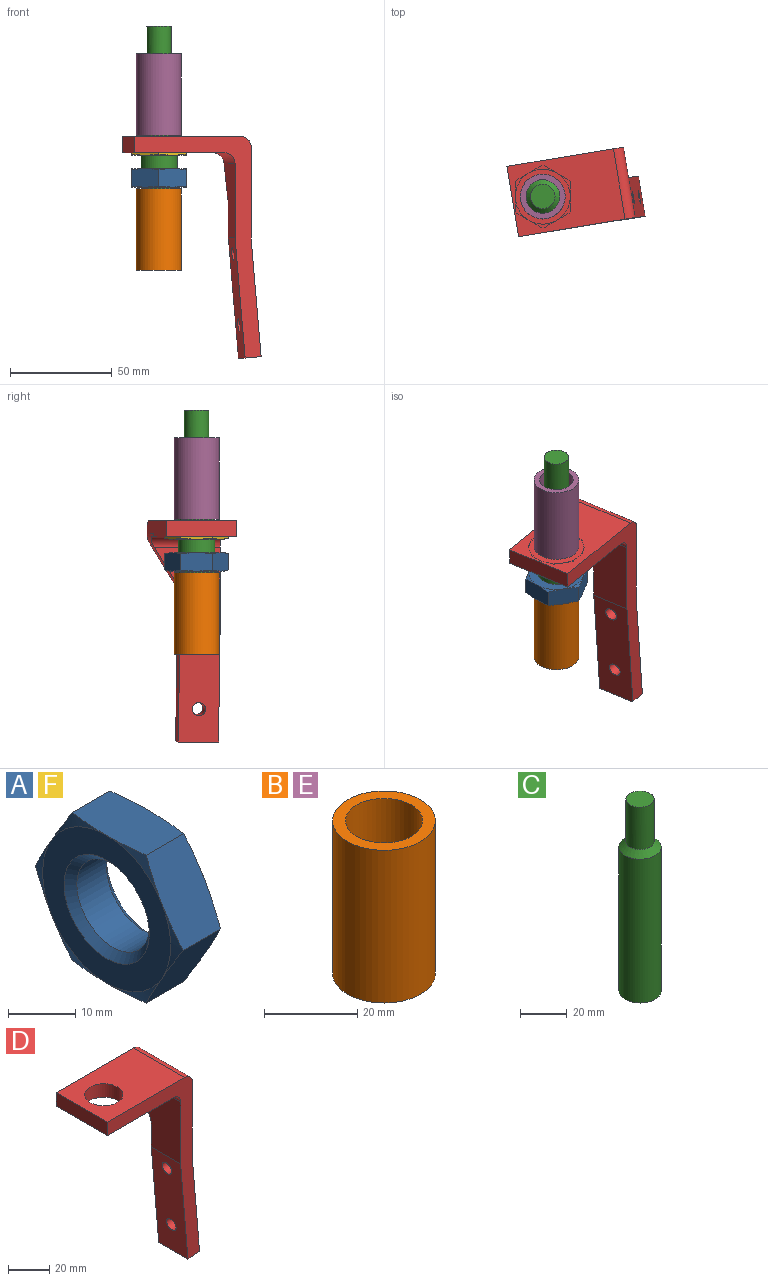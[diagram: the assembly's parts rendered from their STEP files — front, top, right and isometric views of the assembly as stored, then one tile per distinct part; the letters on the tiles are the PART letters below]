
ASSEMBLY  parts=6 mates=5
PART A: 23 faces, bbox 10.2x32.3x32.3 mm
  f0: cone r=13.5mm half-angle=75deg, axis (-1,0,0), area 16.1mm2, adj f14,f17,f22
  f1: cone r=13.5mm half-angle=75deg, axis (-1,0,0), area 16.1mm2, adj f14,f17,f18
  f2: cone r=13.5mm half-angle=75deg, axis (-1,0,0), area 16.1mm2, adj f14,f18,f19
  f3: cone r=13.5mm half-angle=75deg, axis (-1,0,0), area 16.1mm2, adj f14,f19,f20
  f4: cone r=13.5mm half-angle=75deg, axis (-1,0,0), area 16.1mm2, adj f14,f20,f21
  f5: cone r=30.29mm half-angle=75deg, axis (1,0,0), area 16.1mm2, adj f10,f19,f20
  f6: cone r=30.29mm half-angle=75deg, axis (1,0,0), area 16.1mm2, adj f10,f18,f19
  f7: cone r=30.29mm half-angle=75deg, axis (1,0,0), area 16.1mm2, adj f10,f17,f18
  f8: cone r=30.29mm half-angle=75deg, axis (1,0,0), area 16.1mm2, adj f10,f20,f21
  f9: cone r=30.29mm half-angle=75deg, axis (1,0,0), area 16.1mm2, adj f10,f17,f22
  f10: plane 27x27mm, normal (-1,0,0), area 318.1mm2, adj f5,f6,f7,f8,f9,f11,f16
  f11: cone r=9mm half-angle=45deg, axis (-1,0,0), area 100.1mm2, adj f10,f12
  f12: cylinder r=7.65mm len=15.29mm, axis (1,0,0), area 302.4mm2, adj f11,f13
  f13: cone r=7.65mm half-angle=45deg, axis (1,0,0), area 100.1mm2, adj f12,f14
  f14: plane 27x27mm, normal (1,0,0), area 318.1mm2, adj f0,f1,f2,f3,f4,f13,f15
  f15: cone r=13.5mm half-angle=75deg, axis (-1,0,0), area 16.1mm2, adj f14,f21,f22
  f16: cone r=30.29mm half-angle=75deg, axis (1,0,0), area 16.1mm2, adj f10,f21,f22
  f17: plane 16.75x10.16mm, normal (0,0,1), area 134.3mm2, adj f0,f1,f7,f9,f18,f22
  f18: plane 14.66x10.16mm, normal (0,0.87,0.5), area 134.3mm2, adj f1,f2,f6,f7,f17,f19
  f19: plane 14.66x10.16mm, normal (0,0.87,-0.5), area 134.3mm2, adj f2,f3,f5,f6,f18,f20
  f20: plane 16.75x10.16mm, normal (0,0,-1), area 134.3mm2, adj f3,f4,f5,f8,f19,f21
  f21: plane 14.66x10.16mm, normal (0,-0.87,-0.5), area 134.3mm2, adj f4,f8,f15,f16,f20,f22
  f22: plane 14.66x10.16mm, normal (0,-0.87,0.5), area 134.3mm2, adj f0,f9,f15,f16,f17,f21
PART B: 4 faces, bbox 22x22x40 mm
  f0: cylinder r=11mm len=40mm, axis (0,0,-1), area 2764.6mm2, adj f1,f2
  f1: plane 22x22mm, normal (0,0,1), area 166.3mm2, adj f0,f3
  f2: plane 22x22mm, normal (0,0,-1), area 166.3mm2, adj f0,f3
  f3: cylinder r=8.25mm len=40mm, axis (0,0,1), area 2073.5mm2, adj f1,f2
PART C: 5 faces, bbox 18x18x100 mm
  f0: cylinder r=9mm len=75mm, axis (0,0,-1), area 4241.2mm2, adj f1,f4
  f1: plane 18x18mm, normal (0,0,-1), area 254.5mm2, adj f0
  f2: cylinder r=6mm len=22mm, axis (0,0,1), area 829.4mm2, adj f3,f4
  f3: plane 12x12mm, normal (0,0,1), area 113.1mm2, adj f2
  f4: cone r=4mm half-angle=45deg, axis (0,0,-1), area 199.9mm2, adj f0,f2
PART D: 20 faces, bbox 63x35x108.7 mm
  f0: plane 45x35mm, normal (0,0,-1), area 1305.4mm2, adj f1,f7,f10,f11,f17,f18,f19
  f1: cylinder r=5mm len=34.88mm, axis (0,1,0), area 269.2mm2, adj f0,f2,f11,f15,f17
  f2: plane 36.78x32.72mm, normal (-1,0,0), area 866.4mm2, adj f1,f3,f11,f14,f15,f16
  f3: plane 58.91x20mm, normal (-1,0,-0.09), area 1116.1mm2, adj f2,f4,f11,f12,f13,f14
  f4: plane 20x7.97mm, normal (0.09,0,-1), area 160mm2, adj f3,f5,f11,f14
  f5: plane 58.22x20mm, normal (1,0,0.09), area 1102.4mm2, adj f4,f6,f11,f12,f13,f14
  f6: plane 44.78x35mm, normal (1,0,0), area 1141.5mm2, adj f5,f7,f8,f11,f14,f15,f16,f17
  f7: plane 58x8mm, normal (0,1,0), area 428mm2, adj f0,f6,f8,f9,f10,f17,f18
  f8: cylinder r=5mm len=35mm, axis (0,1,0), area 274.9mm2, adj f6,f7,f9,f11
  f9: plane 53x35mm, normal (0,0,1), area 1586.2mm2, adj f7,f8,f10,f11,f19
  f10: plane 35x8mm, normal (-1,0,0), area 280mm2, adj f0,f7,f9,f11
  f11: plane 108.68x63mm, normal (0,-1,0), area 1267.6mm2, adj f0,f1,f2,f3,f4,f5,f6,f8
  f12: cylinder r=3.25mm len=8.52mm, axis (1,0,0.09), area 163.2mm2, adj f3,f5
  f13: cylinder r=3.25mm len=8.5mm, axis (1,0,0.09), area 162.8mm2, adj f3,f5
  f14: plane 72.36x13mm, normal (0,1,0), area 577mm2, adj f2,f3,f4,f5,f6,f16
  f15: plane 19.31x12mm, normal (0,0.85,-0.53), area 181.8mm2, adj f1,f2,f6,f16,f17
  f16: cylinder r=10mm len=8mm, axis (1,0,0), area 44.5mm2, adj f2,f6,f14,f15
  f17: cylinder r=10mm len=20mm, axis (1,0,0), area 68.4mm2, adj f0,f1,f6,f7,f15,f18
  f18: plane 1.53x0.12mm, normal (1,0,0), area 0.1mm2, adj f0,f7,f17
  f19: cylinder r=9.25mm len=18.5mm, axis (0,0,1), area 465mm2, adj f0,f9
PART E: same geometry as B
PART F: same geometry as A
PLACE A rot(axis=(0.71,0,-0.71),180deg) t=(-5.92,-2.32,35.86)mm
PLACE B t=(-5.92,-2.32,-14.08)mm
PLACE C t=(-16.06,-37.89,5.92)mm fixed
PLACE D rot(axis=(0,0,1),9.4deg) t=(-62.55,6.05,-6.5)mm
PLACE E rot(axis=(0,0,-1),90deg) t=(-5.92,-2.32,52.24)mm
PLACE F rot(axis=(-0.71,0,-0.71),180deg) t=(-5.92,-2.32,42.51)mm
MATE revolute B.f0 <-> C.f0  axis (0,0,-1) through (-5.92,-2.32,5.92)mm
MATE cylindrical C.f0 <-> D.f19  axis (0,0,-1) through (-5.92,-2.32,43.42)mm
MATE cylindrical A.f11 <-> D.f19  axis (0,0,-1) through (-5.92,-2.32,34.51)mm
MATE slider E.f0 <-> C.f0  axis (0,0,-1) through (-5.92,-2.32,92.24)mm
MATE cylindrical F.f11 <-> D.f19  axis (0,0,-1) through (-5.92,-2.32,42.51)mm
